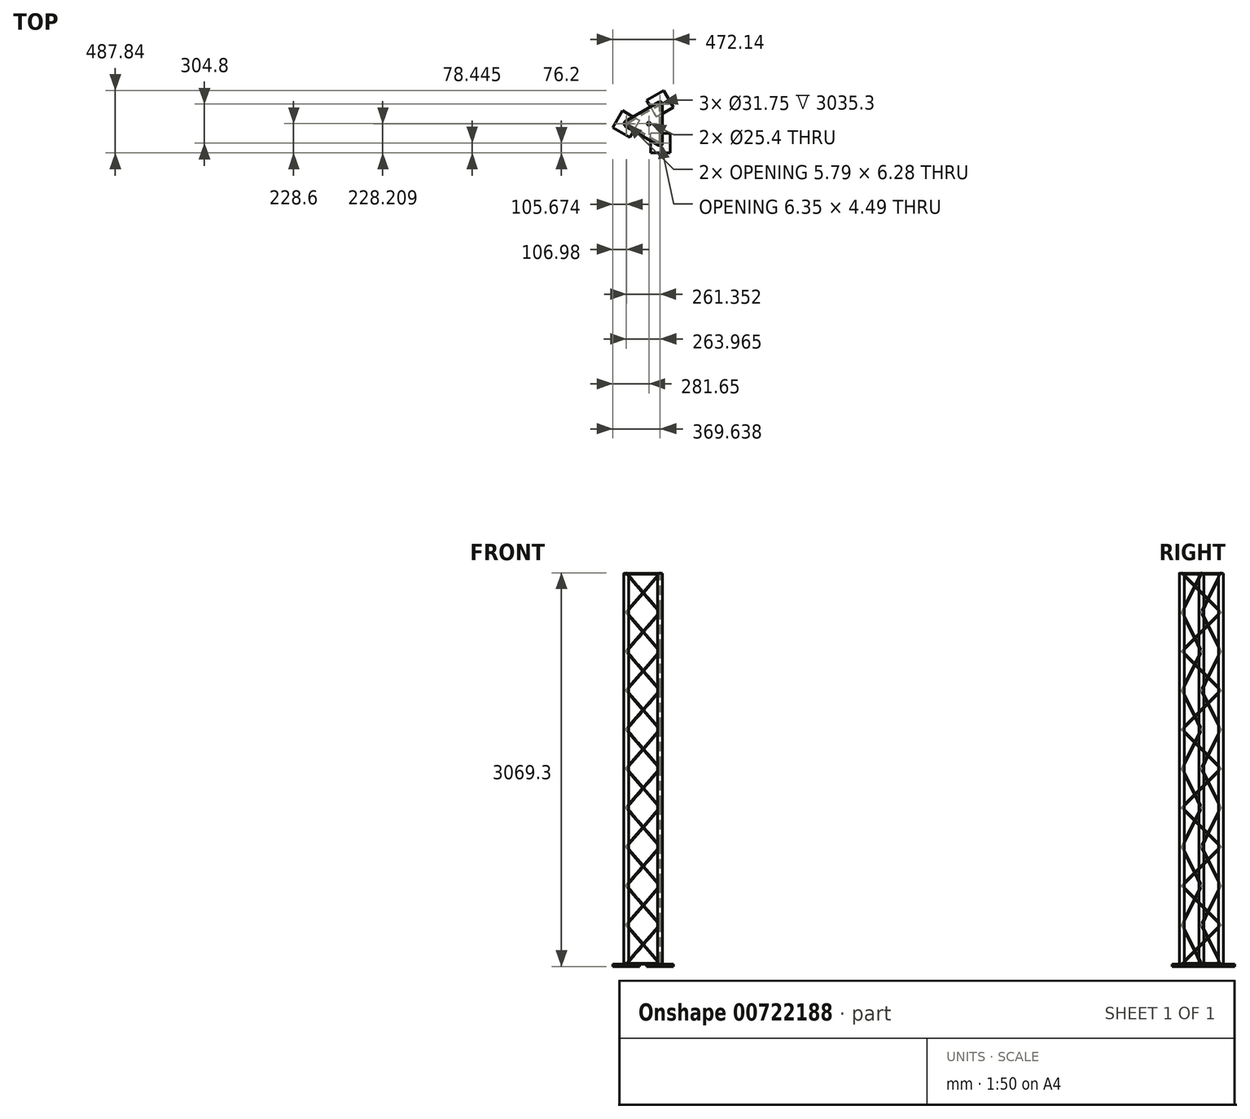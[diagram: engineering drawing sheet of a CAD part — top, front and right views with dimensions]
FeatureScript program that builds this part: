
annotation { "Feature Type Name" : "Feature", "Feature Type Description" : "" }
export const myFeature = defineFeature(function(context is Context, id is Id, definition is map)
    precondition{}
    {
        {
            var Q0;
            Q0=qCreatedBy(makeId("Top.planeOp"),FACE);
            var sketch = newSketch(context, id + "F0", { "sketchPlane" : qUnion([Q0])});
            skCircle(sketch, "E0.cCircle", {"center": v(0, 0) * mm, "radius": 175.98 * mm, "construction": true});
            skLineSegment(sketch, "E0.0", {"start": v(-175.98, 0) * mm, "end": v(87.99, 152.4) * mm, "construction": true});
            skLineSegment(sketch, "E0.1", {"start": v(87.99, 152.4) * mm, "end": v(87.99, -152.4) * mm, "construction": true});
            skLineSegment(sketch, "E0.2", {"start": v(87.99, -152.4) * mm, "end": v(-175.98, 0) * mm, "construction": true});
            skCircle(sketch, "E1", {"center": v(-175.98, 0) * mm, "radius": 19.05 * mm});
            skCircle(sketch, "E2.0", {"center": v(-175.98, 0) * mm, "radius": 15.88 * mm});
            skCircle(sketch, "E3.1.0", {"center": v(87.99, -152.4) * mm, "radius": 15.88 * mm});
            skCircle(sketch, "E3.1.1", {"center": v(87.99, -152.4) * mm, "radius": 19.05 * mm});
            skCircle(sketch, "E3.2.0", {"center": v(87.99, 152.4) * mm, "radius": 15.88 * mm});
            skCircle(sketch, "E3.2.1", {"center": v(87.99, 152.4) * mm, "radius": 19.05 * mm});
            skSolve(sketch);
        }
        {
            var Q0;
            Q0 = qSketchRegion(id + "F0", true);
            extrude(context, id + "F1", {"entities" : qUnion([Q0]), "depth" : 3048 * mm, "offsetDistance" : 25.4 * mm});
        }
        {
            var Q0;
            Q0=makeQuery(id+"F1.opExtrude","CAP_FACE",FACE,{"disambiguationData":[OSD([sQuery(id+"F0.wireOp",EDGE,"E1"),sQuery(id+"F0.wireOp",EDGE,"E2.0")])],"isStart":true});
            var sketch = newSketch(context, id + "F2", { "sketchPlane" : qUnion([Q0])});
            skCircle(sketch, "E4.0", {"center": v(-175.98, 0) * mm, "radius": 19.05 * mm, "construction": true});
            skCircle(sketch, "E5.0", {"center": v(87.99, 152.4) * mm, "radius": 19.05 * mm, "construction": true});
            skCircle(sketch, "E6.0", {"center": v(87.99, -152.4) * mm, "radius": 19.05 * mm, "construction": true});
            skSolve(sketch);
        }
        {
            var Q0;
            Q0=makeQuery(id+"F1.opExtrude","CAP_FACE",FACE,{"disambiguationData":[OSD([sQuery(id+"F0.wireOp",EDGE,"E3.1.0"),sQuery(id+"F0.wireOp",EDGE,"E3.1.1")])],"isStart":false});
            var sketch = newSketch(context, id + "F3", { "sketchPlane" : qUnion([Q0])});
            skCircle(sketch, "E7.0", {"center": v(-175.98, 0) * mm, "radius": 19.05 * mm, "construction": true});
            skCircle(sketch, "E7.1", {"center": v(87.99, -152.4) * mm, "radius": 19.05 * mm, "construction": true});
            skCircle(sketch, "E7.2", {"center": v(87.99, 152.4) * mm, "radius": 19.05 * mm, "construction": true});
            skSolve(sketch);
        }
        {
            var Q0;
            Q0=sQuery(id+"F2.wireOp",VERTEX,"E4.0.center");
            var Q1;
            Q1=sQuery(id+"F2.wireOp",VERTEX,"E5.0.center");
            var Q2;
            Q2=sQuery(id+"F3.wireOp",VERTEX,"E7.1.center");
            cPlane(context, id + "F4", {"entities" : qUnion([Q0, Q1, Q2]), "cplaneType" : CPlaneType.THREE_POINT, "offset" : 25.4 * mm, "width" : 152.4 * mm, "height" : 152.4 * mm});
        }
        {
            var Q0;
            Q0=qCreatedBy(id+"F4.planeOp",FACE);
            var sketch = newSketch(context, id + "F5", { "sketchPlane" : qUnion([Q0])});
            skLineSegment(sketch, "E8", {"start": v(152.4, 0) * mm, "end": v(152.4, 3708.92) * mm, "construction": true});
            skLineSegment(sketch, "E9", {"start": v(-152.4, 3698.2) * mm, "end": v(-152.4, 0) * mm, "construction": true});
            skLineSegment(sketch, "E10", {"start": v(152.4, 0) * mm, "end": v(-152.4, 304.8) * mm});
            skLineSegment(sketch, "E11", {"start": v(-152.4, 304.8) * mm, "end": v(152.4, 609.6) * mm});
            skPoint(sketch, "E12.0", {"position": v(152.4, 0) * mm});
            skPoint(sketch, "E13.0", {"position": v(-152.4, 0) * mm});
            skLineSegment(sketch, "E14.0.1.0", {"start": v(152.4, 609.6) * mm, "end": v(-152.4, 914.4) * mm});
            skLineSegment(sketch, "E14.0.1.1", {"start": v(-152.4, 914.4) * mm, "end": v(152.4, 1219.2) * mm});
            skLineSegment(sketch, "E14.0.2.0", {"start": v(152.4, 1219.2) * mm, "end": v(-152.4, 1524) * mm});
            skLineSegment(sketch, "E14.0.2.1", {"start": v(-152.4, 1524) * mm, "end": v(152.4, 1828.8) * mm});
            skLineSegment(sketch, "E14.0.3.0", {"start": v(152.4, 1828.8) * mm, "end": v(-152.4, 2133.6) * mm});
            skLineSegment(sketch, "E14.0.3.1", {"start": v(-152.4, 2133.6) * mm, "end": v(152.4, 2438.4) * mm});
            skLineSegment(sketch, "E14.0.4.0", {"start": v(152.4, 2438.4) * mm, "end": v(-152.4, 2743.2) * mm});
            skLineSegment(sketch, "E14.0.4.1", {"start": v(-152.4, 2743.2) * mm, "end": v(152.4, 3048) * mm});
            skLineSegment(sketch, "E14.direction1", {"start": v(152.4, 0) * mm, "end": v(177.8, 0) * mm, "construction": true});
            skLineSegment(sketch, "E14.direction2", {"start": v(152.4, 0) * mm, "end": v(152.4, 609.6) * mm, "construction": true});
            skSolve(sketch);
        }
        {
            var Q0;
            Q0=sQuery(id+"F5.wireOp",EDGE,"E10");
            var Q1;
            Q1=sQuery(id+"F5.wireOp",VERTEX,"E12.0");
            cPlane(context, id + "F6", {"entities" : qUnion([Q0, Q1]), "cplaneType" : CPlaneType.CURVE_POINT, "offset" : 25.4 * mm, "width" : 152.4 * mm, "height" : 152.4 * mm});
        }
        {
            var Q0;
            Q0=qCreatedBy(id+"F6.planeOp",FACE);
            var sketch = newSketch(context, id + "F7", { "sketchPlane" : qUnion([Q0])});
            skPoint(sketch, "E15", {"position": v(-139.12, 0) * mm});
            skCircle(sketch, "E16", {"center": v(-139.12, 0) * mm, "radius": 3.18 * mm});
            skSolve(sketch);
        }
        {
            var Q0;
            Q0 = qSketchRegion(id + "F7", true);
            var Q1;
            Q1 = qConstructionFilter(qBodyType(qCreatedBy(id + "F5" ,EDGE), BodyType.WIRE), ConstructionObject.NO);
            sweep(context, id + "F8", {"profiles" : qUnion([Q0]), "path" : qUnion([Q1])});
        }
        {
            var Q0;
            Q0=qCreatedBy(makeId("Front.planeOp"),FACE);
            var sketch = newSketch(context, id + "F9", { "sketchPlane" : qUnion([Q0])});
            skLineSegment(sketch, "E17", {"start": v(0, 0) * mm, "end": v(0, 663.8) * mm, "construction": true});
            skSolve(sketch);
        }
        {
            var Q0;
            Q0=makeQuery(id+"F8.opSweep","SWEPT_BODY",BODY,{"disambiguationData":[OSD([sQuery(id+"F5.wireOp",EDGE,"E14.0.4.1"),sQuery(id+"F7.wireOp",EDGE,"E16")])]});
            var Q1;
            Q1=sQuery(id+"F9.wireOp",EDGE,"E17");
            circularPattern(context, id + "F10", {"entities" : qUnion([Q0]), "axis" : qUnion([Q1]), "angle" : 360 * degree, "instanceCount" : 3, "equalSpace" : true});
        }
        {
            var Q0;
            Q0=makeQuery(id+"F1.opExtrude","CAP_FACE",FACE,{"disambiguationData":[OSD([sQuery(id+"F0.wireOp",EDGE,"E3.1.0"),sQuery(id+"F0.wireOp",EDGE,"E3.1.1")])],"isStart":true});
            var sketch = newSketch(context, id + "F11", { "sketchPlane" : qUnion([Q0])});
            skCircle(sketch, "E18.0", {"center": v(87.99, 152.4) * mm, "radius": 19.05 * mm});
            skCircle(sketch, "E19.0", {"center": v(-175.98, 0) * mm, "radius": 19.05 * mm});
            skCircle(sketch, "E20.0", {"center": v(87.99, -152.4) * mm, "radius": 19.05 * mm});
            skLineSegment(sketch, "E21", {"start": v(107.04, 152.4) * mm, "end": v(107.04, -152.4) * mm});
            skLineSegment(sketch, "E22", {"start": v(78.46, -168.9) * mm, "end": v(-185.5, -16.5) * mm});
            skLineSegment(sketch, "E23", {"start": v(-185.5, 16.5) * mm, "end": v(78.46, 168.9) * mm});
            skCircle(sketch, "E24", {"center": v(0, 0) * mm, "radius": 12.7 * mm});
            skSolve(sketch);
        }
        {
            var Q0;
            Q0 = qSketchRegion(id + "F11", true);
            extrude(context, id + "F12", {"entities" : qUnion([Q0]), "oppositeDirection" : true, "depth" : 6.35 * mm, "offsetDistance" : 25.4 * mm});
        }
        {
            var Q0;
            Q0=makeQuery(id+"F12.opExtrude","SWEPT_BODY",BODY,{"disambiguationData":[OSD([sQuery(id+"F11.wireOp",EDGE,"E18.0"),sQuery(id+"F11.wireOp",EDGE,"E19.0"),sQuery(id+"F11.wireOp",EDGE,"E20.0"),sQuery(id+"F11.wireOp",EDGE,"E21"),sQuery(id+"F11.wireOp",EDGE,"E22"),sQuery(id+"F11.wireOp",EDGE,"E23"),sQuery(id+"F11.wireOp",EDGE,"E24")])]});
            transform(context, id + "F13", {"entities" : qUnion([Q0]), "transformType" : TransformType.TRANSLATION_3D, "dx" : 0 * mm, "dy" : 0 * mm, "dz" : 3041.65 * mm, "makeCopy" : true});
        }
        {
            var Q0;
            Q0=makeQuery(id+"F1.opExtrude","SWEPT_BODY",BODY,{"disambiguationData":[OSD([sQuery(id+"F0.wireOp",EDGE,"E3.1.0"),sQuery(id+"F0.wireOp",EDGE,"E3.1.1")])]});
            var Q1;
            Q1=makeQuery(id+"F1.opExtrude","SWEPT_BODY",BODY,{"disambiguationData":[OSD([sQuery(id+"F0.wireOp",EDGE,"E3.2.0"),sQuery(id+"F0.wireOp",EDGE,"E3.2.1")])]});
            var Q2;
            Q2=makeQuery(id+"F8.opSweep","SWEPT_BODY",BODY,{"disambiguationData":[OSD([sQuery(id+"F5.wireOp",EDGE,"E14.0.4.1"),sQuery(id+"F7.wireOp",EDGE,"E16")])]});
            var Q3;
            Q3=makeQuery(id+"F10.opPattern","COPY",BODY,{"derivedFrom":makeQuery(id+"F8.opSweep","SWEPT_BODY",BODY,{"disambiguationData":[OSD([sQuery(id+"F5.wireOp",EDGE,"E14.0.4.1"),sQuery(id+"F7.wireOp",EDGE,"E16")])]}),"instanceName":"1"});
            var Q4;
            Q4=makeQuery(id+"F10.opPattern","COPY",BODY,{"derivedFrom":makeQuery(id+"F8.opSweep","SWEPT_BODY",BODY,{"disambiguationData":[OSD([sQuery(id+"F5.wireOp",EDGE,"E14.0.4.1"),sQuery(id+"F7.wireOp",EDGE,"E16")])]}),"instanceName":"2"});
            var Q5;
            Q5=makeQuery(id+"F12.opExtrude","SWEPT_BODY",BODY,{"disambiguationData":[OSD([sQuery(id+"F11.wireOp",EDGE,"E18.0"),sQuery(id+"F11.wireOp",EDGE,"E19.0"),sQuery(id+"F11.wireOp",EDGE,"E20.0"),sQuery(id+"F11.wireOp",EDGE,"E21"),sQuery(id+"F11.wireOp",EDGE,"E22"),sQuery(id+"F11.wireOp",EDGE,"E23"),sQuery(id+"F11.wireOp",EDGE,"E24")])]});
            booleanBodies(context, id + "F14", {"operationType" : BooleanOperationType.UNION, "tools" : qUnion([Q0, Q1, Q2, Q3, Q4, Q5])});
        }
        {
            var Q0;
            Q0=makeQuery(id+"F1.opExtrude","SWEPT_BODY",BODY,{"disambiguationData":[OSD([sQuery(id+"F0.wireOp",EDGE,"E1"),sQuery(id+"F0.wireOp",EDGE,"E2.0")])]});
            var Q1;
            Q1=makeQuery(id+"F1.opExtrude","SWEPT_BODY",BODY,{"disambiguationData":[OSD([sQuery(id+"F0.wireOp",EDGE,"E3.1.0"),sQuery(id+"F0.wireOp",EDGE,"E3.1.1")])]});
            booleanBodies(context, id + "F15", {"operationType" : BooleanOperationType.UNION, "tools" : qUnion([Q0, Q1])});
        }
        {
            var Q0;
            Q0=makeQuery(id+"F1.opExtrude","SWEPT_BODY",BODY,{"disambiguationData":[OSD([sQuery(id+"F0.wireOp",EDGE,"E1"),sQuery(id+"F0.wireOp",EDGE,"E2.0")])]});
            var Q1;
            Q1=makeQuery(id+"F13.opPattern","COPY",BODY,{"derivedFrom":makeQuery(id+"F12.opExtrude","SWEPT_BODY",BODY,{"disambiguationData":[OSD([sQuery(id+"F11.wireOp",EDGE,"E18.0"),sQuery(id+"F11.wireOp",EDGE,"E19.0"),sQuery(id+"F11.wireOp",EDGE,"E20.0"),sQuery(id+"F11.wireOp",EDGE,"E21"),sQuery(id+"F11.wireOp",EDGE,"E22"),sQuery(id+"F11.wireOp",EDGE,"E23"),sQuery(id+"F11.wireOp",EDGE,"E24")])]}),"instanceName":"1"});
            booleanBodies(context, id + "F16", {"operationType" : BooleanOperationType.UNION, "tools" : qUnion([Q0, Q1])});
        }
        {
            var Q0;
            Q0=makeQuery(id+"F15.opBoolean","MERGE",FACE,{"derivedFrom":[makeQuery(id+"F1.opExtrude","CAP_FACE",FACE,{"disambiguationData":[OSD([sQuery(id+"F0.wireOp",EDGE,"E1"),sQuery(id+"F0.wireOp",EDGE,"E2.0")])],"isStart":true}),makeQuery(id+"F14.opBoolean","MERGE",FACE,{"derivedFrom":[makeQuery(id+"F1.opExtrude","CAP_FACE",FACE,{"disambiguationData":[OSD([sQuery(id+"F0.wireOp",EDGE,"E3.1.0"),sQuery(id+"F0.wireOp",EDGE,"E3.1.1")])],"isStart":true}),makeQuery(id+"F1.opExtrude","CAP_FACE",FACE,{"disambiguationData":[OSD([sQuery(id+"F0.wireOp",EDGE,"E3.2.0"),sQuery(id+"F0.wireOp",EDGE,"E3.2.1")])],"isStart":true}),makeQuery(id+"F12.opExtrude","CAP_FACE",FACE,{"disambiguationData":[OSD([sQuery(id+"F11.wireOp",EDGE,"E18.0"),sQuery(id+"F11.wireOp",EDGE,"E19.0"),sQuery(id+"F11.wireOp",EDGE,"E20.0"),sQuery(id+"F11.wireOp",EDGE,"E21"),sQuery(id+"F11.wireOp",EDGE,"E22"),sQuery(id+"F11.wireOp",EDGE,"E23"),sQuery(id+"F11.wireOp",EDGE,"E24")])],"isStart":true})]})]});
            var sketch = newSketch(context, id + "F17", { "sketchPlane" : qUnion([Q0])});
            skCircle(sketch, "E25.0", {"center": v(87.99, 152.4) * mm, "radius": 19.05 * mm, "construction": true});
            skLineSegment(sketch, "E26.bottom", {"start": v(167.36, 228.6) * mm, "end": v(14.96, 228.6) * mm});
            skLineSegment(sketch, "E26.top", {"start": v(167.36, 76.2) * mm, "end": v(14.96, 76.2) * mm});
            skLineSegment(sketch, "E26.left", {"start": v(167.36, 228.6) * mm, "end": v(167.36, 76.2) * mm});
            skLineSegment(sketch, "E26.right", {"start": v(14.96, 228.6) * mm, "end": v(14.96, 76.2) * mm});
            skPoint(sketch, "E26.middle", {"position": v(91.16, 152.4) * mm});
            skSolve(sketch);
        }
        {
            var Q0;
            Q0 = qSketchRegion(id + "F17", true);
            extrude(context, id + "F18", {"entities" : qUnion([Q0]), "depth" : 19.05 * mm, "offsetDistance" : 25.4 * mm});
        }
        {
            var Q0;
            Q0=makeQuery(id+"F18.opExtrude","SWEPT_BODY",BODY,{"disambiguationData":[OSD([sQuery(id+"F17.wireOp",EDGE,"E26.bottom"),sQuery(id+"F17.wireOp",EDGE,"E26.top"),sQuery(id+"F17.wireOp",EDGE,"E26.left"),sQuery(id+"F17.wireOp",EDGE,"E26.right")])]});
            var Q1;
            Q1=makeQuery(id+"F12.opExtrude","CAP_EDGE",EDGE,{"disambiguationData":[OSD([sQuery(id+"F11.wireOp",EDGE,"E24")])],"isStart":true});
            circularPattern(context, id + "F19", {"entities" : qUnion([Q0]), "axis" : qUnion([Q1]), "angle" : 360 * degree, "instanceCount" : 3, "equalSpace" : true});
        }
    });
